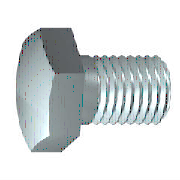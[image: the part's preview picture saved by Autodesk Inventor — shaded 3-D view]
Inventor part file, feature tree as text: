
AUTODESK INVENTOR PART (.ipt)
format: ipt  version: 2021 (Build 250183000, 183)  size: 221,696 bytes
history: native  units: mm (DEFAULTED — no unit token found)
features: sketch x4, other x3, revolve x2, extrude x2, fillet x1
ambient origin geometry x8: Origin, YZ Plane, XZ Plane, XY Plane, X Axis, Y Axis, Z Axis, Center Point
bodies: Solid1 (feature_tree)
feature tree (12):
  revolve  "Revolution1"  Angle=45.0deg
  extrude  "Extrusion1"  TaperAngle=60.0deg  [1 undecoded]
  revolve  "Revolution2"  Angle=30.0deg
  extrude  "Extrusion2"  TaperAngle=0.0deg  [1 undecoded]
  other  "MSC_A1"
  other  "MSC_PF1"
  other  "MSC_PT1"
  fillet  "Fillet1"  [1 undecoded]
  sketch  "Sketch2"  dims[d3=30.0deg d5=45.0deg]
  sketch  "Sketch3"  dims[d8=90.0deg d9=60.0deg]
  sketch  "Sketch4"  dims[d13=0.0mm d14=30.0deg]
  sketch  "Sketch5"  dims[d16=90.0deg d18=0.0mm d22=0.0mm d23=0.0mm d25=0.0mm d26=0.0mm d27=13.5mm d28=1.5mm d29=0.0mm d30=0.6mm d31=0.0mm]
note: 3 required parameter values undecoded (feature->parameter linkage not recoverable at this tier; creation-order binding heuristic only, values carry confidence <= 0.55)
